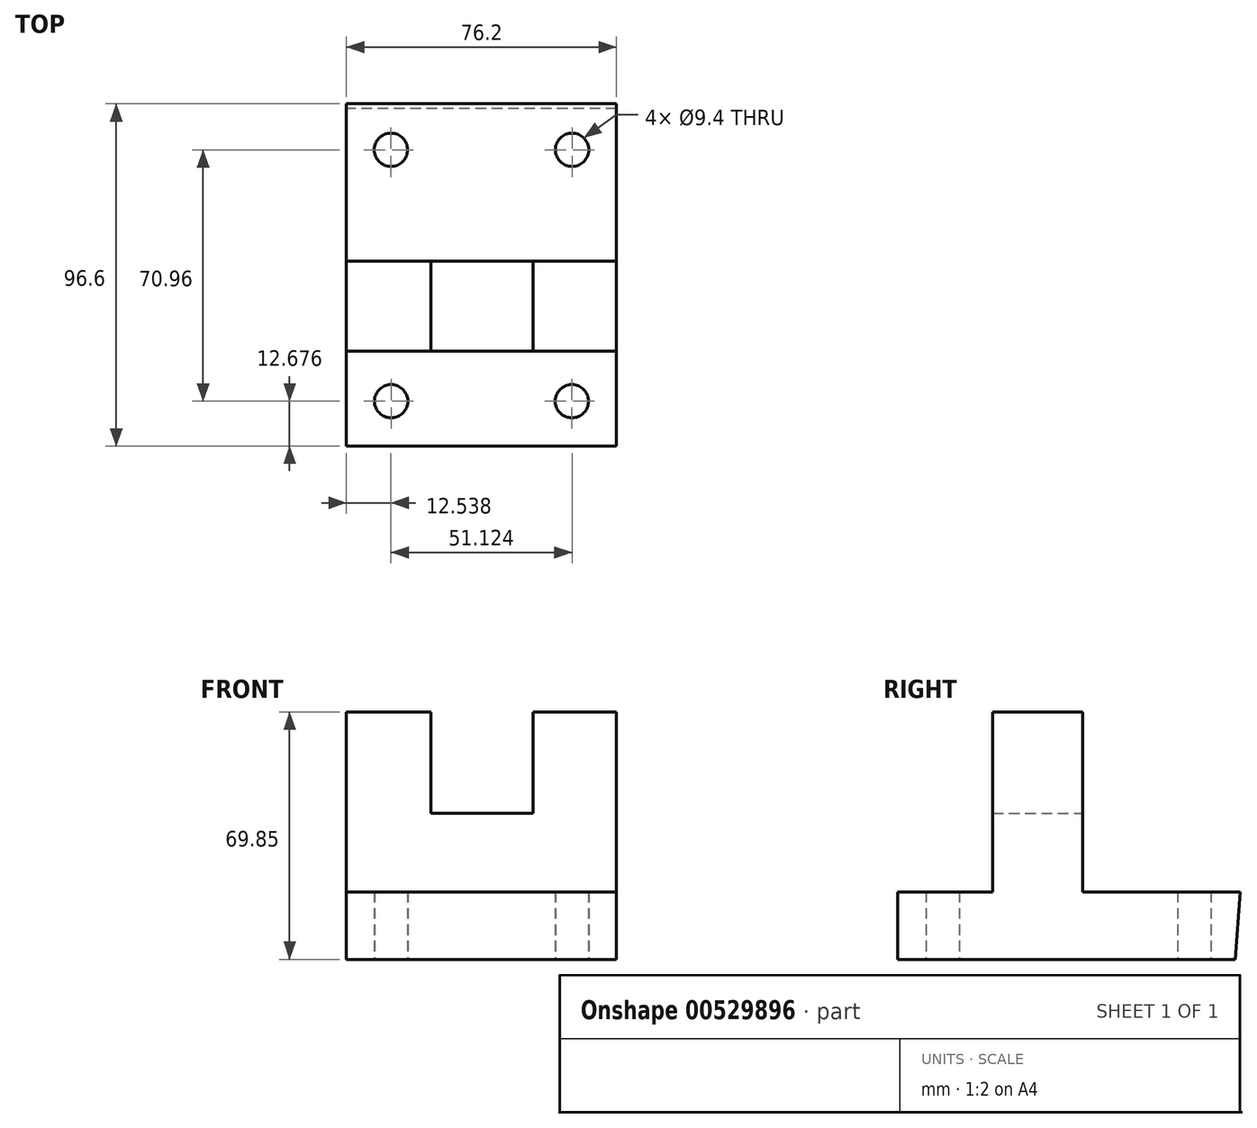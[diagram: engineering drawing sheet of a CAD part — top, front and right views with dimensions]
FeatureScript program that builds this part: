
annotation { "Feature Type Name" : "Feature", "Feature Type Description" : "" }
export const myFeature = defineFeature(function(context is Context, id is Id, definition is map)
    precondition{}
    {
        {
            var Q0;
            Q0=qCreatedBy(makeId("Front.planeOp"),FACE);
            var sketch = newSketch(context, id + "F0", { "sketchPlane" : qUnion([Q0])});
            skLineSegment(sketch, "E0", {"start": v(38.1, 0) * mm, "end": v(-38.1, 0) * mm});
            skLineSegment(sketch, "E1", {"start": v(-38.1, 0) * mm, "end": v(-38.1, 69.85) * mm});
            skLineSegment(sketch, "E2", {"start": v(-38.1, 69.85) * mm, "end": v(-14.27, 69.85) * mm});
            skLineSegment(sketch, "E3", {"start": v(-14.27, 69.85) * mm, "end": v(-14.27, 41.27) * mm});
            skLineSegment(sketch, "E4", {"start": v(-14.27, 41.27) * mm, "end": v(14.56, 41.27) * mm});
            skLineSegment(sketch, "E5", {"start": v(14.56, 41.28) * mm, "end": v(14.56, 69.85) * mm});
            skLineSegment(sketch, "E6", {"start": v(14.56, 69.85) * mm, "end": v(38.1, 69.85) * mm});
            skLineSegment(sketch, "E7", {"start": v(38.1, 69.85) * mm, "end": v(38.1, 0) * mm});
            skSolve(sketch);
        }
        {
            var Q0;
            Q0 = qSketchRegion(id + "F0", true);
            extrude(context, id + "F1", {"entities" : qUnion([Q0]), "depth" : 25.4 * mm, "offsetDistance" : 25.4 * mm});
        }
        {
            var Q0;
            Q0=qCreatedBy(makeId("Right.planeOp"),FACE);
            var sketch = newSketch(context, id + "F2", { "sketchPlane" : qUnion([Q0])});
            skPoint(sketch, "E8.orphan", {"position": v(44.45, 19.05) * mm});
            skPoint(sketch, "E9.end.orphan", {"position": v(96.4, 19.05) * mm});
            skPoint(sketch, "E10.orphan", {"position": v(95.05, 0) * mm});
            skPoint(sketch, "E11.start.orphan", {"position": v(0, 19.05) * mm});
            skPoint(sketch, "E12.start.orphan", {"position": v(-22.02, 19.05) * mm});
            skLineSegment(sketch, "E13", {"start": v(0, 0) * mm, "end": v(43.1, 0) * mm});
            skLineSegment(sketch, "E14", {"start": v(43.1, 0) * mm, "end": v(44.45, 19.05) * mm});
            skLineSegment(sketch, "E15", {"start": v(0, 19.05) * mm, "end": v(44.45, 19.05) * mm});
            skLineSegment(sketch, "E16", {"start": v(-52.15, 19.05) * mm, "end": v(-52.15, 0) * mm});
            skPoint(sketch, "E16.startSnap0", {"position": v(22.23, 19.05) * mm});
            skLineSegment(sketch, "E17", {"start": v(-52.15, 0) * mm, "end": v(0, 0) * mm});
            skLineSegment(sketch, "E18", {"start": v(43.1, 0) * mm, "end": v(-52.15, 0) * mm});
            skLineSegment(sketch, "E19", {"start": v(-52.15, 19.05) * mm, "end": v(0, 19.05) * mm});
            skSolve(sketch);
        }
        {
            var Q0;
            Q0 = qSketchRegion(id + "F2", true);
            extrude(context, id + "F3", {"entities" : qUnion([Q0]), "operationType" : NewBodyOperationType.ADD, "endBound" : BoundingType.SYMMETRIC, "depth" : 76.2 * mm, "offsetDistance" : 25.4 * mm});
        }
        {
            var Q0;
            Q0=qCreatedBy(makeId("Top.planeOp"),FACE);
            var sketch = newSketch(context, id + "F4", { "sketchPlane" : qUnion([Q0])});
            skCircle(sketch, "E20", {"center": v(-25.56, 31.49) * mm, "radius": 4.7 * mm});
            skCircle(sketch, "E21", {"center": v(-25.5, -39.47) * mm, "radius": 4.7 * mm});
            skCircle(sketch, "E22.MirrorC", {"center": v(25.5, -39.47) * mm, "radius": 4.7 * mm});
            skCircle(sketch, "E23.MirrorC", {"center": v(25.56, 31.49) * mm, "radius": 4.7 * mm});
            skSolve(sketch);
        }
        {
            var Q0;
            Q0=sQuery(id+"F4.wireOp",VERTEX,"E21.center");
            var Q1;
            Q1=sQuery(id+"F4.wireOp",VERTEX,"E22.MirrorC.center");
            var Q2;
            Q2=sQuery(id+"F4.wireOp",VERTEX,"E23.MirrorC.center");
            var Q3;
            Q3=sQuery(id+"F4.wireOp",VERTEX,"E20.center");
            var Q4;
            Q4=makeQuery(id+"F1.opExtrude","SWEPT_BODY",BODY,{"disambiguationData":[OSD([sQuery(id+"F0.wireOp",EDGE,"E0"),sQuery(id+"F0.wireOp",EDGE,"E1"),sQuery(id+"F0.wireOp",EDGE,"E2"),sQuery(id+"F0.wireOp",EDGE,"E3"),sQuery(id+"F0.wireOp",EDGE,"E4"),sQuery(id+"F0.wireOp",EDGE,"E5"),sQuery(id+"F0.wireOp",EDGE,"E6"),sQuery(id+"F0.wireOp",EDGE,"E7")])]});
            hole(context, id + "F5", {"style" : HoleStyle.SIMPLE, "endStyle" : HoleEndStyle.THROUGH, "oppositeDirection" : true, "holeDiameter" : 9.4 * mm, "isTappedThrough" : true, "tappedDepth" : 12.7 * mm, "tapClearance" : 3, "locations" : qUnion([Q0, Q1, Q2, Q3]), "scope" : qUnion([Q4])});
        }
    });
